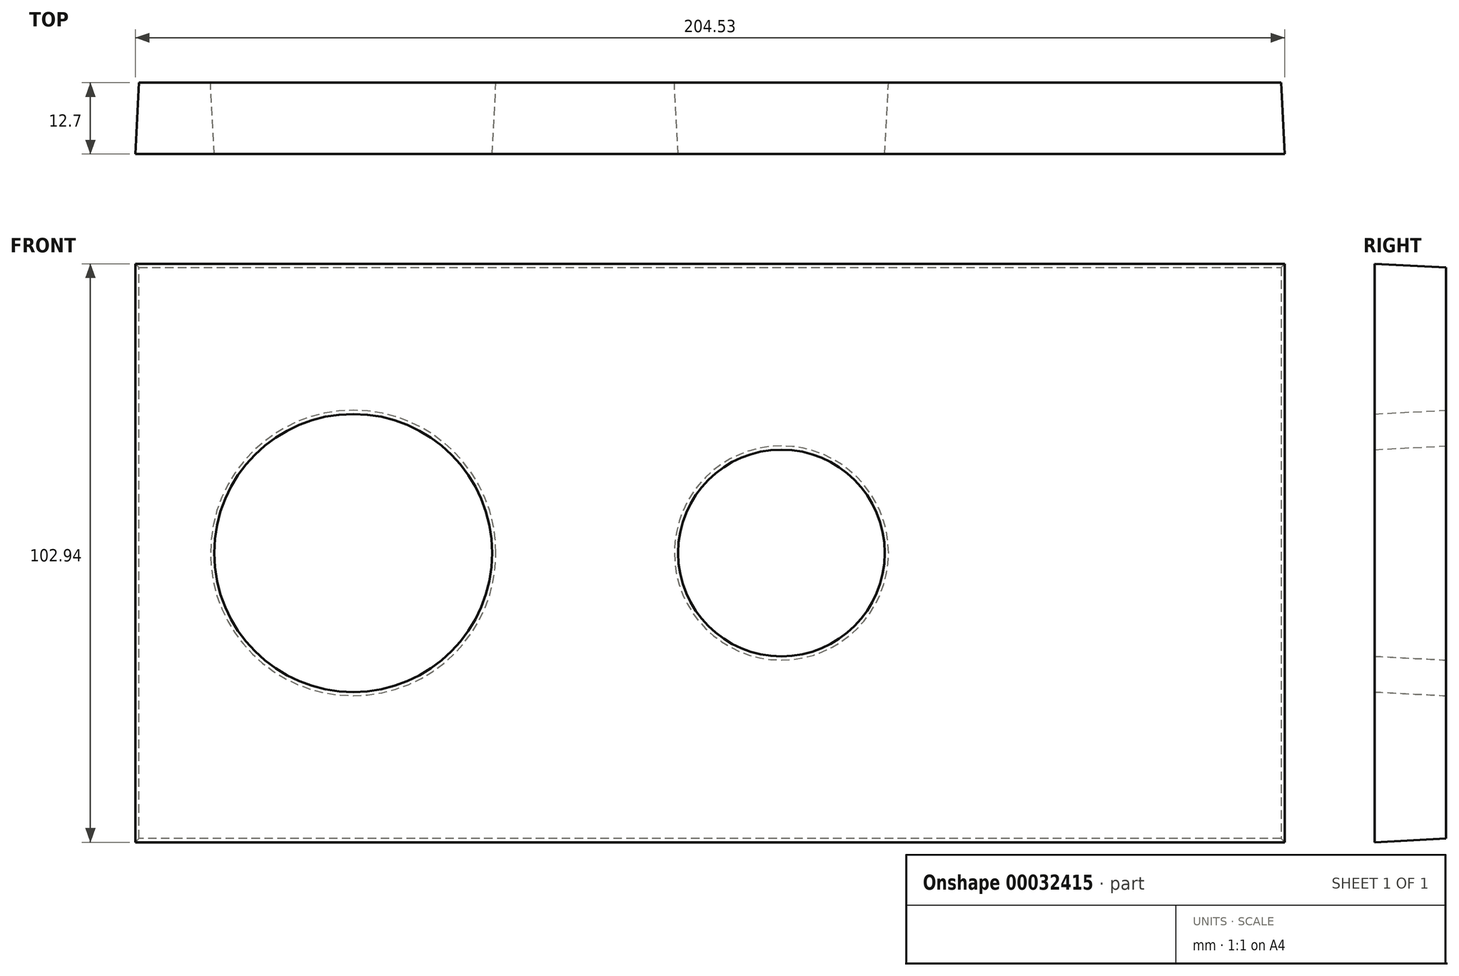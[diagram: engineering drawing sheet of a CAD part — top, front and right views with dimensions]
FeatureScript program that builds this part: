
annotation { "Feature Type Name" : "Feature", "Feature Type Description" : "" }
export const myFeature = defineFeature(function(context is Context, id is Id, definition is map)
    precondition{}
    {
        {
            var Q0;
            Q0=qCreatedBy(makeId("Front.planeOp"),FACE);
            var sketch = newSketch(context, id + "F0", { "sketchPlane" : qUnion([Q0])});
            skLineSegment(sketch, "E0.bottom", {"start": v(76.4, 50.8) * mm, "end": v(-126.8, 50.8) * mm});
            skLineSegment(sketch, "E0.top", {"start": v(76.4, -50.8) * mm, "end": v(-126.8, -50.8) * mm});
            skLineSegment(sketch, "E0.left", {"start": v(76.4, 50.8) * mm, "end": v(76.4, -50.8) * mm});
            skLineSegment(sketch, "E0.right", {"start": v(-126.8, 50.8) * mm, "end": v(-126.8, -50.8) * mm});
            skCircle(sketch, "E1", {"center": v(-12.5, 0) * mm, "radius": 19.05 * mm});
            skCircle(sketch, "E2", {"center": v(-88.7, 0) * mm, "radius": 25.4 * mm});
            skSolve(sketch);
        }
        {
            var Q0;
            Q0=makeQuery(id+"F0.imprint","IMPRINT",FACE,{"disambiguationData":[TD([[makeQuery(id+"F0.imprint","IMPRINT",EDGE,{"derivedFrom":sQuery(id+"F0.wireOp",EDGE,"E0.bottom")}),1.0]])]});
            extrude(context, id + "F1", {"entities" : qUnion([Q0]), "depth" : 12.7 * mm, "hasDraft" : true, "draftAngle" : 3 * degree});
        }
    });
